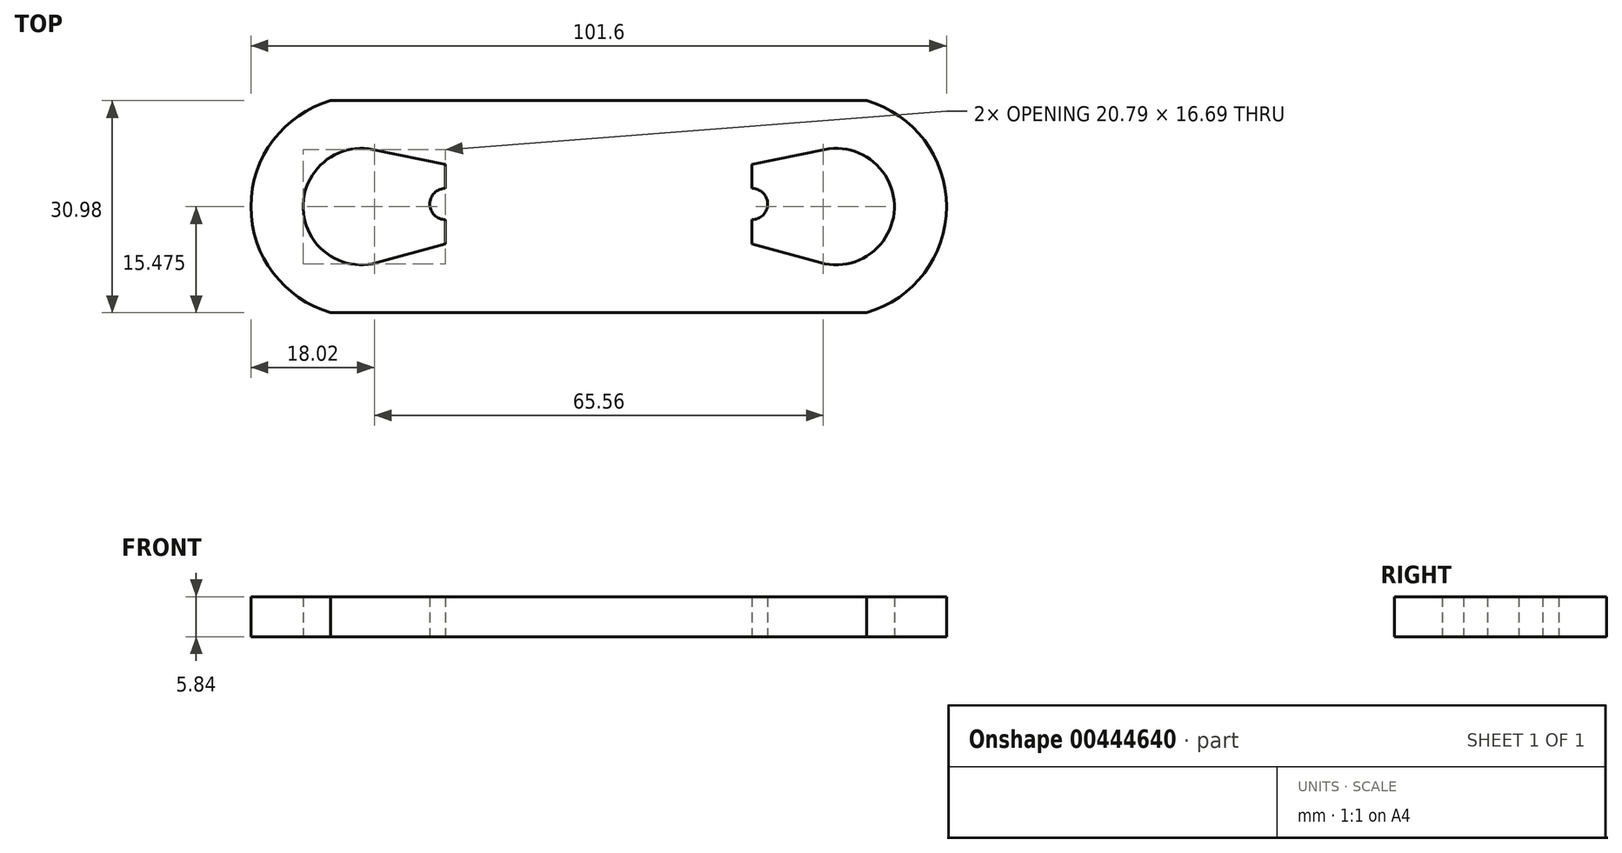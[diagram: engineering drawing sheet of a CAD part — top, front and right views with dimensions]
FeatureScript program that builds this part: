
annotation { "Feature Type Name" : "Feature", "Feature Type Description" : "" }
export const myFeature = defineFeature(function(context is Context, id is Id, definition is map)
    precondition{}
    {
        {
            var Q0;
            Q0=qCreatedBy(makeId("Top.planeOp"),FACE);
            var sketch = newSketch(context, id + "F0", { "sketchPlane" : qUnion([Q0])});
            skLineSegment(sketch, "E0.bottom", {"start": v(-39.14, 15.5) * mm, "end": v(39.14, 15.5) * mm});
            skLineSegment(sketch, "E0.top", {"start": v(-39.14, -15.5) * mm, "end": v(39.14, -15.5) * mm});
            skPoint(sketch, "E0.middle", {"position": v(0, 0) * mm});
            skPoint(sketch, "E1.middle", {"position": v(34.68, 0) * mm});
            skArc(sketch, "E2", {"start": v(32.41, -8.2) * mm, "mid": v(43.17, -0.3) * mm, "end": v(32.99, 8.33) * mm});
            skLineSegment(sketch, "E3.left", {"start": v(22.39, 6.18) * mm, "end": v(22.39, 2.66) * mm});
            skPoint(sketch, "E3.middle", {"position": v(11.5, 0) * mm});
            skPoint(sketch, "E3.bottom.end.orphan", {"position": v(0.61, 5.43) * mm});
            skPoint(sketch, "E4.orphan", {"position": v(0.61, -6.18) * mm});
            skLineSegment(sketch, "E5", {"start": v(22.39, 6.18) * mm, "end": v(32.99, 8.33) * mm});
            skLineSegment(sketch, "E6", {"start": v(22.39, -5.43) * mm, "end": v(32.41, -8.2) * mm});
            skArc(sketch, "E7", {"start": v(22.39, -1.9) * mm, "mid": v(24.67, 0.38) * mm, "end": v(22.39, 2.66) * mm});
            skLineSegment(sketch, "E8.trimOffspring", {"start": v(22.39, -1.9) * mm, "end": v(22.39, -5.43) * mm});
            skPoint(sketch, "E9", {"position": v(43.17, -0.3) * mm});
            skArc(sketch, "E10.MirrorCS", {"start": v(-32.41, -8.2) * mm, "mid": v(-43.17, -0.3) * mm, "end": v(-32.99, 8.33) * mm});
            skLineSegment(sketch, "E11.MirrorCS", {"start": v(-22.39, 6.18) * mm, "end": v(-32.99, 8.33) * mm});
            skLineSegment(sketch, "E12.MirrorCS", {"start": v(-22.39, 6.18) * mm, "end": v(-22.39, 2.66) * mm});
            skArc(sketch, "E13.MirrorCS", {"start": v(-22.39, -1.9) * mm, "mid": v(-24.67, 0.38) * mm, "end": v(-22.39, 2.66) * mm});
            skLineSegment(sketch, "E14.MirrorCS", {"start": v(-22.39, -1.9) * mm, "end": v(-22.39, -5.43) * mm});
            skLineSegment(sketch, "E15.MirrorCS", {"start": v(-22.39, -5.43) * mm, "end": v(-32.41, -8.2) * mm});
            skLineSegment(sketch, "E16", {"start": v(32.99, 8.33) * mm, "end": v(32.99, 15.5) * mm});
            skLineSegment(sketch, "E17", {"start": v(32.41, -8.2) * mm, "end": v(32.41, -15.5) * mm});
            skArc(sketch, "E18.0", {"start": v(39.14, -15.5) * mm, "mid": v(50.8, 0) * mm, "end": v(39.14, 15.5) * mm});
            skPoint(sketch, "E19.orphan", {"position": v(50.8, 15.5) * mm});
            skPoint(sketch, "E20.orphan", {"position": v(50.8, -15.5) * mm});
            skArc(sketch, "E21.MirrorCS", {"start": v(-39.14, -15.5) * mm, "mid": v(-50.8, 0) * mm, "end": v(-39.14, 15.5) * mm});
            skPoint(sketch, "E22.trimOffspring.end.orphan", {"position": v(-50.8, -15.5) * mm});
            skPoint(sketch, "E23", {"position": v(-50.8, 0) * mm});
            skPoint(sketch, "E24", {"position": v(50.8, 0) * mm});
            skPoint(sketch, "E25.orphan", {"position": v(-50.8, 15.5) * mm});
            skSolve(sketch);
        }
        {
            var Q0;
            Q0=makeQuery(id+"F0.imprint","IMPRINT",FACE,{"disambiguationData":[TD([[makeQuery(id+"F0.imprint","IMPRINT",EDGE,{"derivedFrom":sQuery(id+"F0.wireOp",EDGE,"E0.bottom")}),-1.0]])]});
            var Q1;
            Q1=makeQuery(id+"F0.imprint","IMPRINT",FACE,{"disambiguationData":[TD([[makeQuery(id+"F0.imprint","IMPRINT",EDGE,{"derivedFrom":sQuery(id+"F0.wireOp",EDGE,"E3.left")}),-1.0]])]});
            extrude(context, id + "F1", {"entities" : qUnion([Q0, Q1]), "depth" : 5.84 * mm});
        }
    });
